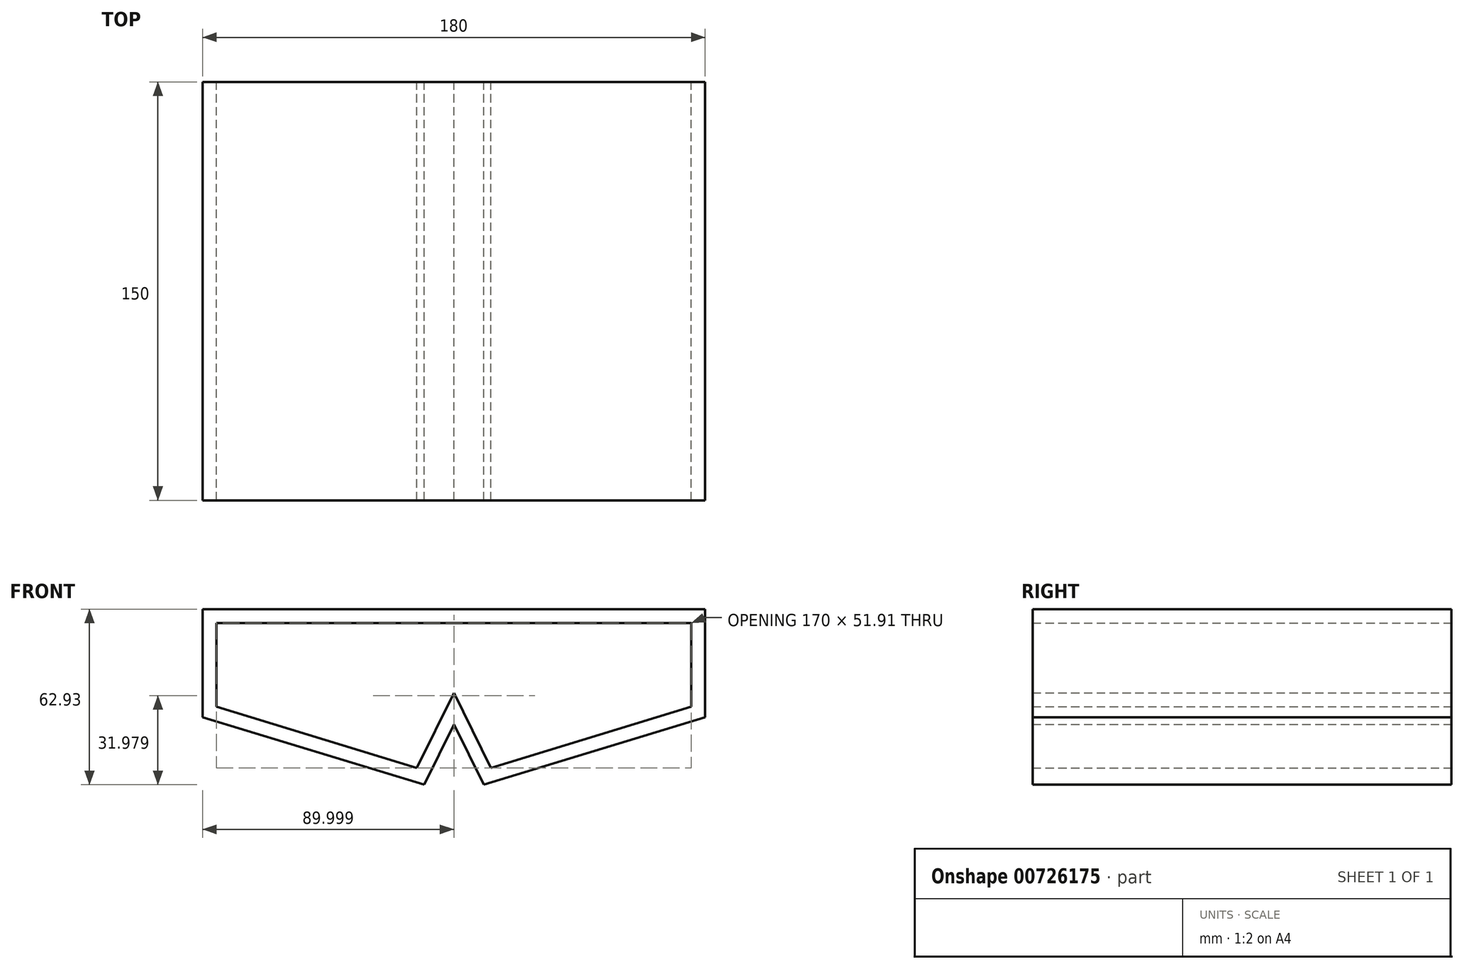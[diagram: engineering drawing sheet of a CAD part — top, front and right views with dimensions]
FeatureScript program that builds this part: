
annotation { "Feature Type Name" : "Feature", "Feature Type Description" : "" }
export const myFeature = defineFeature(function(context is Context, id is Id, definition is map)
    precondition{}
    {
        {
            var Q0;
            Q0=qCreatedBy(makeId("Front.planeOp"),FACE);
            var sketch = newSketch(context, id + "F0", { "sketchPlane" : qUnion([Q0])});
            skLineSegment(sketch, "E0.0", {"start": v(9.74, -2.67) * mm, "end": v(89.07, 21.56) * mm});
            skLineSegment(sketch, "E0.1", {"start": v(9.74, -2.67) * mm, "end": v(-0.93, 18.96) * mm});
            skLineSegment(sketch, "E0.2", {"start": v(89.07, 21.56) * mm, "end": v(89.07, 60.26) * mm});
            skLineSegment(sketch, "E0.3", {"start": v(-11.6, -2.67) * mm, "end": v(-0.93, 18.96) * mm});
            skLineSegment(sketch, "E0.4", {"start": v(-0.93, 60.26) * mm, "end": v(89.07, 60.26) * mm});
            skLineSegment(sketch, "E0.5", {"start": v(-0.93, 60.26) * mm, "end": v(-90.93, 60.26) * mm});
            skLineSegment(sketch, "E0.6", {"start": v(-90.93, 21.56) * mm, "end": v(-90.93, 60.26) * mm});
            skLineSegment(sketch, "E0.7", {"start": v(-11.6, -2.67) * mm, "end": v(-90.93, 21.56) * mm});
            skLineSegment(sketch, "E1.0", {"start": v(12.34, 3.36) * mm, "end": v(84.07, 25.26) * mm});
            skLineSegment(sketch, "E1.1", {"start": v(12.34, 3.36) * mm, "end": v(-0.93, 30.26) * mm});
            skLineSegment(sketch, "E1.2", {"start": v(84.07, 25.26) * mm, "end": v(84.07, 55.26) * mm});
            skLineSegment(sketch, "E1.3", {"start": v(-14.2, 3.36) * mm, "end": v(-0.93, 30.26) * mm});
            skLineSegment(sketch, "E1.4", {"start": v(-0.93, 55.26) * mm, "end": v(84.07, 55.26) * mm});
            skLineSegment(sketch, "E1.5", {"start": v(-0.93, 55.26) * mm, "end": v(-85.93, 55.26) * mm});
            skLineSegment(sketch, "E1.6", {"start": v(-85.93, 25.26) * mm, "end": v(-85.93, 55.26) * mm});
            skLineSegment(sketch, "E1.7", {"start": v(-14.2, 3.36) * mm, "end": v(-85.93, 25.26) * mm});
            skSolve(sketch);
        }
        {
            var Q0;
            Q0=qSketchRegion(id+"F0",true);
            extrude(context, id + "F1", {"entities" : qUnion([Q0]), "depth" : 150 * mm, "offsetDistance" : 25 * mm});
        }
    });
